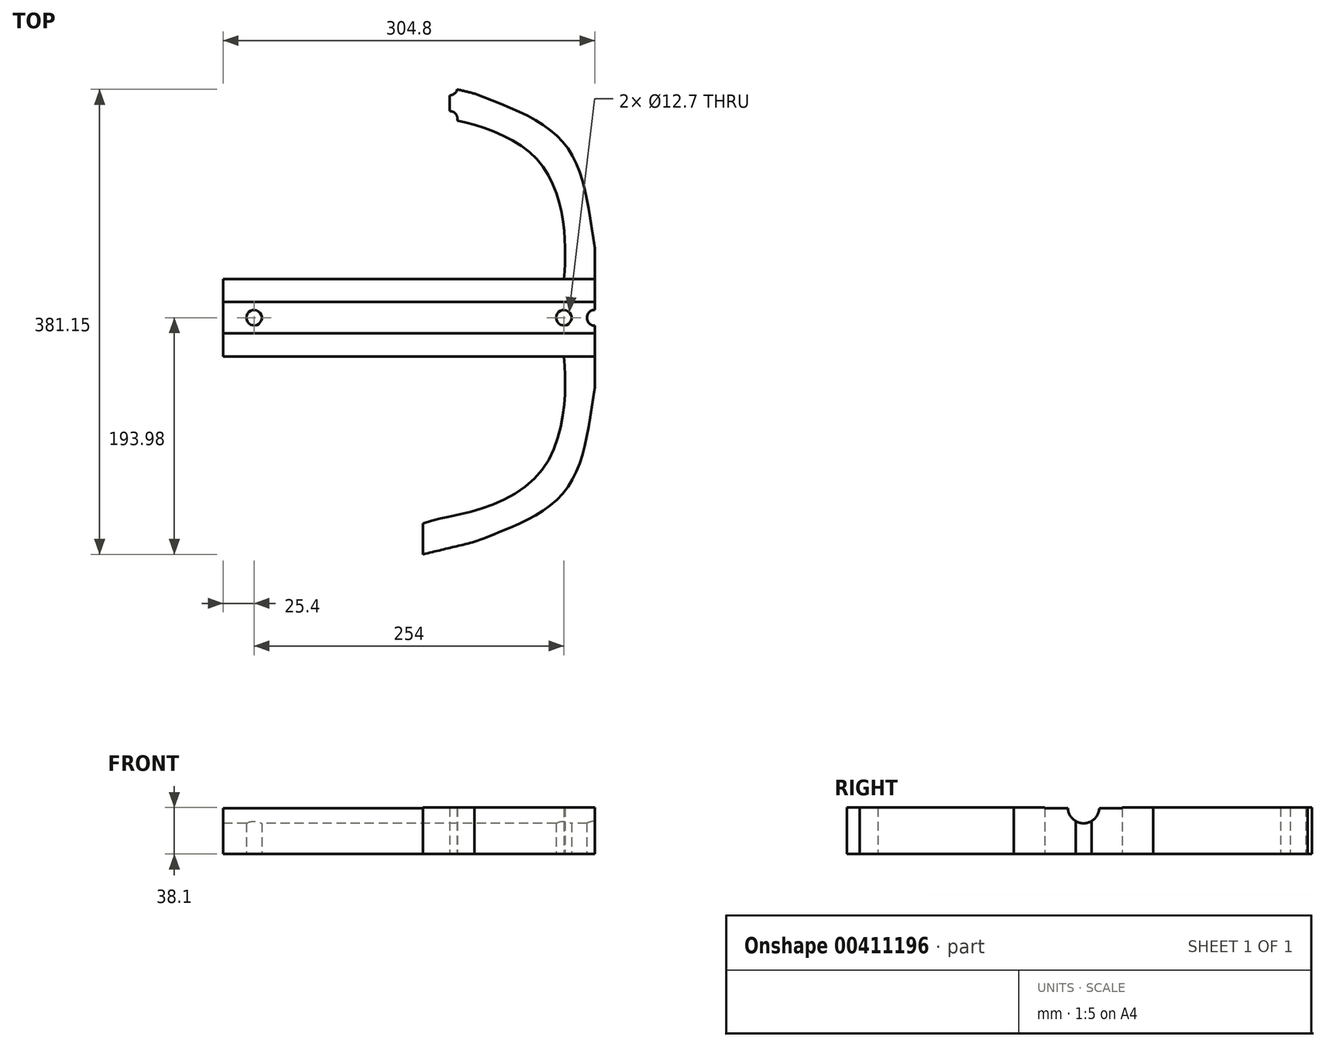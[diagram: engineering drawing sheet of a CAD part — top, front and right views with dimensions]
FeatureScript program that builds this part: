
annotation { "Feature Type Name" : "Feature", "Feature Type Description" : "" }
export const myFeature = defineFeature(function(context is Context, id is Id, definition is map)
    precondition{}
    {
        {
            var Q0;
            Q0=qCreatedBy(makeId("Right.planeOp"),FACE);
            var sketch = newSketch(context, id + "F0", { "sketchPlane" : qUnion([Q0])});
            skLineSegment(sketch, "E0", {"start": v(-31.75, 0) * mm, "end": v(31.75, 0) * mm});
            skLineSegment(sketch, "E1", {"start": v(0, 0) * mm, "end": v(0, 38.1) * mm, "construction": true});
            skArc(sketch, "E2", {"start": v(-12.85, 37.67) * mm, "mid": v(0, 25.24) * mm, "end": v(12.85, 37.67) * mm});
            skLineSegment(sketch, "E3", {"start": v(31.75, 37.67) * mm, "end": v(12.85, 37.67) * mm});
            skLineSegment(sketch, "E4", {"start": v(-31.75, 37.67) * mm, "end": v(-12.85, 37.67) * mm});
            skLineSegment(sketch, "E5", {"start": v(31.75, 0) * mm, "end": v(31.75, 37.67) * mm});
            skLineSegment(sketch, "E6", {"start": v(-31.75, 0) * mm, "end": v(-31.75, 37.67) * mm});
            skSolve(sketch);
        }
        {
            var Q0;
            Q0=makeQuery(id+"F0.imprint","IMPRINT",FACE,{"disambiguationData":[TD([[makeQuery(id+"F0.imprint","IMPRINT",EDGE,{"derivedFrom":sQuery(id+"F0.wireOp",EDGE,"E0")}),1.0]])]});
            extrude(context, id + "F1", {"entities" : qUnion([Q0]), "depth" : 304.8 * mm});
        }
        {
            var Q0;
            Q0=makeQuery(id+"F1.opExtrude","SWEPT_FACE",FACE,{"disambiguationData":[OSD([sQuery(id+"F0.wireOp",EDGE,"E0")])]});
            var sketch = newSketch(context, id + "F2", { "sketchPlane" : qUnion([Q0])});
            skArc(sketch, "E7", {"start": v(304.8, 6.5) * mm, "mid": v(298.3, 0) * mm, "end": v(304.8, -6.5) * mm});
            skLineSegment(sketch, "E8", {"start": v(304.8, 6.5) * mm, "end": v(304.8, -6.5) * mm});
            skSolve(sketch);
        }
        {
            var Q0;
            Q0 = qSketchRegion(id + "F2", true);
            extrude(context, id + "F3", {"entities" : qUnion([Q0]), "operationType" : NewBodyOperationType.REMOVE, "endBound" : BoundingType.THROUGH_ALL, "oppositeDirection" : true, "depth" : 25.4 * mm});
        }
        {
            var Q0;
            Q0=makeQuery(id+"F1.opExtrude","SWEPT_FACE",FACE,{"disambiguationData":[OSD([sQuery(id+"F0.wireOp",EDGE,"E0")])]});
            var sketch = newSketch(context, id + "F4", { "sketchPlane" : qUnion([Q0])});
            skCircle(sketch, "E9", {"center": v(279.4, 0) * mm, "radius": 6.35 * mm});
            skCircle(sketch, "E10", {"center": v(25.4, 0) * mm, "radius": 6.35 * mm});
            skSolve(sketch);
        }
        {
            var Q0;
            Q0=sQuery(id+"F4.wireOp",VERTEX,"E10.center");
            var Q1;
            Q1=sQuery(id+"F4.wireOp",VERTEX,"E9.center");
            var Q2;
            Q2=makeQuery(id+"F1.opExtrude","SWEPT_BODY",BODY,{"disambiguationData":[OSD([sQuery(id+"F0.wireOp",EDGE,"E0"),sQuery(id+"F0.wireOp",EDGE,"eqOhWqWR-fqMG-14e0-ChVJ-K62lo4gadKtR"),sQuery(id+"F0.wireOp",EDGE,"1ujJTKUa-DzRU-oCY2-0nf8-GRjmj3KIVbKP"),sQuery(id+"F0.wireOp",EDGE,"2NO2QR3h-vpVU-I8qZ-9noV-CONNcpex9s8j"),sQuery(id+"F0.wireOp",EDGE,"FqcB4VFG-GcSZ-unYt-IBjK-BweuuOEmwhqD"),sQuery(id+"F0.wireOp",EDGE,"E2")])]});
            hole(context, id + "F5", {"style" : HoleStyle.SIMPLE, "endStyle" : HoleEndStyle.THROUGH, "holeDiameter" : 12.7 * mm, "isTappedThrough" : true, "tappedDepth" : 12.7 * mm, "tapClearance" : 3, "locations" : qUnion([Q0, Q1]), "scope" : qUnion([Q2])});
        }
        {
            var Q0;
            Q0=makeQuery(id+"F1.opExtrude","SWEPT_FACE",FACE,{"disambiguationData":[OSD([sQuery(id+"F0.wireOp",EDGE,"E0")])]});
            var sketch = newSketch(context, id + "F6", { "sketchPlane" : qUnion([Q0])});
            skLineSegment(sketch, "E11", {"start": v(304.8, 31.75) * mm, "end": v(304.8, 6.35) * mm});
            skLineSegment(sketch, "E12", {"start": v(304.8, 31.75) * mm, "end": v(304.8, 57.15) * mm});
            skFitSpline(sketch, "E13", {"points": [v(304.8, 57.15) * mm, v(280.31, 141.97) * mm, v(206.11, 183.69) * mm], "startDerivative": vector(-30.8, 186.97) * mm, "endDerivative": vector(-166.97, 65.25) * mm});
            skFitSpline(sketch, "E14", {"points": [v(206.11, 183.69) * mm, v(163.92, 193.98) * mm], "startDerivative": vector(-42.55, 10.68) * mm, "endDerivative": vector(-44.73, 11.25) * mm});
            skLineSegment(sketch, "E15", {"start": v(298.3, 0) * mm, "end": v(179.86, 0) * mm, "construction": true});
            skFitSpline(sketch, "E16.MirrorCS", {"points": [v(304.8, -57.15) * mm, v(280.31, -141.97) * mm, v(206.11, -183.69) * mm], "startDerivative": vector(-30.8, -186.97) * mm, "endDerivative": vector(-166.97, -65.25) * mm});
            skFitSpline(sketch, "E17.MirrorCS", {"points": [v(206.11, -183.69) * mm, v(163.92, -193.98) * mm], "startDerivative": vector(-42.55, -10.68) * mm, "endDerivative": vector(-44.73, -11.25) * mm});
            skFitSpline(sketch, "E18", {"points": [v(279.4, 31.75) * mm, v(279.46, 72.67) * mm, v(259.8, 126.98) * mm, v(205.56, 158.29) * mm, v(163.92, 168.58) * mm], "startDerivative": vector(16.28, 176.2) * mm, "endDerivative": vector(-155.32, 56.78) * mm});
            skLineSegment(sketch, "E19", {"start": v(163.92, 193.98) * mm, "end": v(163.92, 168.58) * mm});
            skFitSpline(sketch, "E20.MirrorCS", {"points": [v(279.4, -31.75) * mm, v(279.46, -72.67) * mm, v(259.8, -126.98) * mm, v(205.56, -158.29) * mm, v(163.92, -168.58) * mm], "startDerivative": vector(16.28, -176.2) * mm, "endDerivative": vector(-155.32, -56.78) * mm});
            skLineSegment(sketch, "E21.MirrorCS", {"start": v(163.92, -193.98) * mm, "end": v(163.92, -168.58) * mm});
            skLineSegment(sketch, "E22", {"start": v(304.8, -57.15) * mm, "end": v(304.8, 31.75) * mm});
            skLineSegment(sketch, "E23", {"start": v(185.82, -188.63) * mm, "end": v(185.82, -162.95) * mm});
            skLineSegment(sketch, "E24", {"start": v(192, -187.15) * mm, "end": v(179.64, -190.12) * mm, "construction": true});
            skLineSegment(sketch, "E25", {"start": v(179.6, -164.27) * mm, "end": v(192.03, -161.63) * mm, "construction": true});
            skArc(sketch, "E26", {"start": v(191.93, -187.25) * mm, "mid": v(184.33, -182.43) * mm, "end": v(179.64, -190.12) * mm});
            skArc(sketch, "E27", {"start": v(179.6, -164.27) * mm, "mid": v(187.15, -169.23) * mm, "end": v(192.03, -161.63) * mm});
            skSolve(sketch);
        }
        {
            var Q0;
            {var subQ1=sQuery(id+"F6.wireOp",EDGE,"E16.MirrorCS");Q0=makeQuery(id+"F6.imprint","IMPRINT",FACE,{"disambiguationData":[TD([[makeQuery(id+"F6.imprint","IMPRINT",EDGE,{"derivedFrom":subQ1}),-1.0]])]});}
            var Q1;
            {var subQ1=sQuery(id+"F6.wireOp",EDGE,"E12");Q1=makeQuery(id+"F6.imprint","IMPRINT",FACE,{"disambiguationData":[TD([[makeQuery(id+"F6.imprint","IMPRINT",EDGE,{"derivedFrom":subQ1}),1.0]])]});}
            extrude(context, id + "F7", {"entities" : qUnion([Q0, Q1]), "operationType" : NewBodyOperationType.ADD, "oppositeDirection" : true, "depth" : 38.1 * mm});
        }
    });
